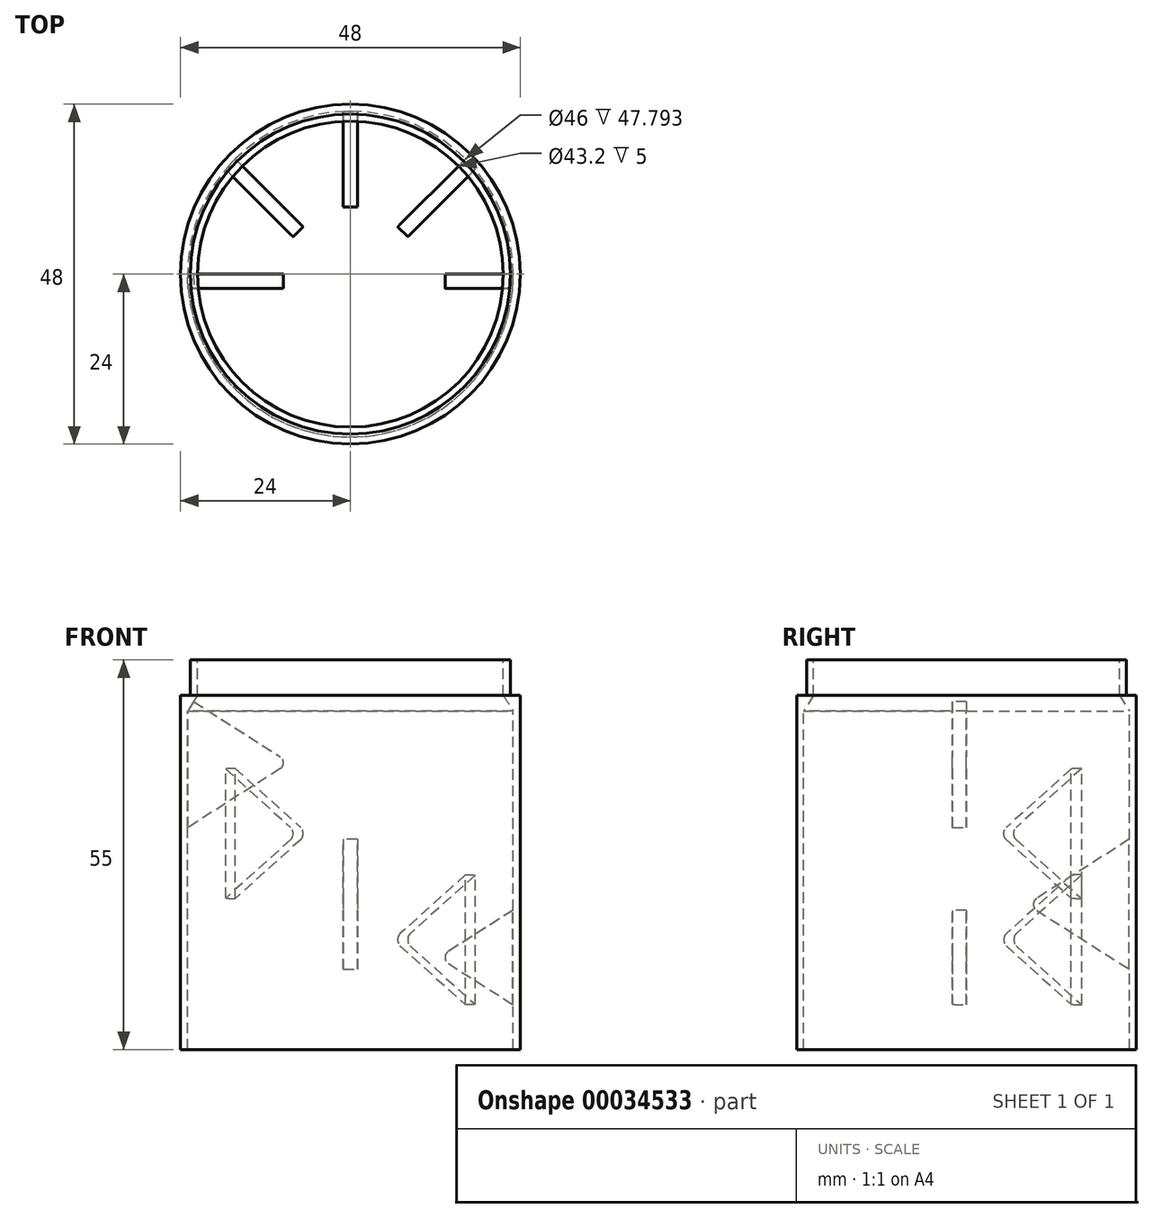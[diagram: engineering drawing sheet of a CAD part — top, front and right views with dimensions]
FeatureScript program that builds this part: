
annotation { "Feature Type Name" : "Feature", "Feature Type Description" : "" }
export const myFeature = defineFeature(function(context is Context, id is Id, definition is map)
    precondition{}
    {
        {
            var Q0;
            Q0=qCreatedBy(makeId("Top.planeOp"),FACE);
            var sketch = newSketch(context, id + "F0", { "sketchPlane" : qUnion([Q0])});
            skCircle(sketch, "E0", {"center": v(0, 0) * mm, "radius": 24 * mm});
            skSolve(sketch);
        }
        {
            var Q0;
            Q0=makeQuery(id+"F0.imprint","IMPRINT",FACE,{"disambiguationData":[TD([[makeQuery(id+"F0.imprint","IMPRINT",EDGE,{"derivedFrom":sQuery(id+"F0.wireOp",EDGE,"E0")}),1.0]])]});
            extrude(context, id + "F1", {"entities" : qUnion([Q0]), "depth" : 50 * mm});
        }
        {
            var Q0;
            Q0=makeQuery(id+"F1.opExtrude","CAP_FACE",FACE,{"disambiguationData":[OSD([sQuery(id+"F0.wireOp",EDGE,"E0")])],"isStart":false});
            var sketch = newSketch(context, id + "F2", { "sketchPlane" : qUnion([Q0])});
            skCircle(sketch, "E1", {"center": v(0, 0) * mm, "radius": 23 * mm});
            skSolve(sketch);
        }
        {
            var Q0;
            Q0=qSketchRegion(id+"F2",true);
            extrude(context, id + "F3", {"entities" : qUnion([Q0]), "operationType" : NewBodyOperationType.REMOVE, "endBound" : BoundingType.THROUGH_ALL, "oppositeDirection" : true, "depth" : 25 * mm});
        }
        {
            var Q0;
            Q0=qCreatedBy(makeId("Front.planeOp"),FACE);
            var sketch = newSketch(context, id + "F4", { "sketchPlane" : qUnion([Q0])});
            skLineSegment(sketch, "E2", {"start": v(0, 0) * mm, "end": v(0, 50) * mm});
            skLineSegment(sketch, "E3.0", {"start": v(-23.5, 50) * mm, "end": v(-23.5, 47) * mm});
            skLineSegment(sketch, "E4", {"start": v(-23.5, 50) * mm, "end": v(-22.6, 50) * mm});
            skLineSegment(sketch, "E5", {"start": v(-22.6, 50) * mm, "end": v(-22.6, 55) * mm});
            skLineSegment(sketch, "E6", {"start": v(-22.6, 55) * mm, "end": v(-21.6, 55) * mm});
            skLineSegment(sketch, "E7", {"start": v(-21.6, 55) * mm, "end": v(-21.6, 50) * mm});
            skLineSegment(sketch, "E8", {"start": v(-21.6, 50) * mm, "end": v(-23.5, 47) * mm});
            skLineSegment(sketch, "E9", {"start": v(-24, 50) * mm, "end": v(-23.5, 50) * mm});
            skSolve(sketch);
        }
        {
            var Q0;
            Q0=qSketchRegion(id+"F4",true);
            var Q1;
            Q1=makeQuery(id+"F3.boolean.opBoolean","COPY",FACE,{"derivedFrom":makeQuery(id+"F3.opExtrude","SWEPT_FACE",FACE,{"disambiguationData":[OSD([sQuery(id+"F2.wireOp",EDGE,"E1")])]})});
            revolve(context, id + "F5", {"operationType" : NewBodyOperationType.ADD, "entities" : qUnion([Q0]), "axis" : qUnion([Q1]), "revolveType" : RevolveType.FULL});
        }
        {
            var Q0;
            Q0=qCreatedBy(makeId("Right.planeOp"),FACE);
            var sketch = newSketch(context, id + "F6", { "sketchPlane" : qUnion([Q0])});
            skCircle(sketch, "E10", {"center": v(0, 27.55) * mm, "radius": 3 * mm});
            skLineSegment(sketch, "E11.rect.bottom", {"start": v(-3, 21.55) * mm, "end": v(3, 21.55) * mm});
            skLineSegment(sketch, "E11.rect.top", {"start": v(-3, 27.55) * mm, "end": v(3, 27.55) * mm});
            skLineSegment(sketch, "E11.rect.left", {"start": v(-3, 21.55) * mm, "end": v(-3, 27.55) * mm});
            skLineSegment(sketch, "E11.rect.right", {"start": v(3, 21.55) * mm, "end": v(3, 27.55) * mm});
            skPoint(sketch, "E11.rect.middle", {"position": v(0, 24.55) * mm});
            skSolve(sketch);
        }
        {
            var Q0;
            Q0=qCreatedBy(makeId("Front.planeOp"),FACE);
            var sketch = newSketch(context, id + "F7", { "sketchPlane" : qUnion([Q0])});
            skLineSegment(sketch, "E12", {"start": v(0, 0) * mm, "end": v(0, 55) * mm, "construction": true});
            skPoint(sketch, "E13", {"position": v(0, 55) * mm});
            skSolve(sketch);
        }
        {
            var Q0;
            Q0=qCreatedBy(makeId("Top.planeOp"),FACE);
            var sketch = newSketch(context, id + "F8", { "sketchPlane" : qUnion([Q0])});
            skLineSegment(sketch, "E14", {"start": v(0, 0) * mm, "end": v(-23.5, 0) * mm, "construction": true});
            skLineSegment(sketch, "E15", {"start": v(0, 0) * mm, "end": v(-16.62, 16.62) * mm, "construction": true});
            skLineSegment(sketch, "E16", {"start": v(0, 0) * mm, "end": v(0, 23.5) * mm, "construction": true});
            skLineSegment(sketch, "E17.MirrorCS", {"start": v(0, 0) * mm, "end": v(16.62, 16.62) * mm, "construction": true});
            skLineSegment(sketch, "E18.MirrorCS", {"start": v(0, 0) * mm, "end": v(23.5, 0) * mm, "construction": true});
            skSolve(sketch);
        }
        {
            var Q0;
            Q0=qCreatedBy(makeId("Front.planeOp"),FACE);
            var sketch = newSketch(context, id + "F9", { "sketchPlane" : qUnion([Q0])});
            skLineSegment(sketch, "E19", {"start": v(-23.5, 50) * mm, "end": v(-8.59, 40.5) * mm});
            skLineSegment(sketch, "E20", {"start": v(-8.59, 40.5) * mm, "end": v(-23.5, 31) * mm});
            skLineSegment(sketch, "E21", {"start": v(-23.5, 31) * mm, "end": v(-23.5, 50) * mm});
            skLineSegment(sketch, "E22", {"start": v(-8.59, 40.5) * mm, "end": v(-23.5, 40.5) * mm, "construction": true});
            skPoint(sketch, "E23.0", {"position": v(-23.5, 0) * mm});
            skLineSegment(sketch, "E24", {"start": v(-23.5, 0) * mm, "end": v(-23.5, 50) * mm, "construction": true});
            skPoint(sketch, "E25.0", {"position": v(23.5, 0) * mm});
            skLineSegment(sketch, "E26", {"start": v(23.5, 0) * mm, "end": v(23.5, 20) * mm, "construction": true});
            skLineSegment(sketch, "E27", {"start": v(23.5, 20) * mm, "end": v(23.5, 6) * mm});
            skLineSegment(sketch, "E28", {"start": v(23.5, 20) * mm, "end": v(12.51, 13) * mm});
            skLineSegment(sketch, "E29", {"start": v(12.51, 13) * mm, "end": v(23.5, 6) * mm});
            skLineSegment(sketch, "E30", {"start": v(23.5, 13) * mm, "end": v(12.51, 13) * mm, "construction": true});
            skSolve(sketch);
        }
        {
            var Q0;
            Q0=makeQuery(id+"F9.imprint","IMPRINT",FACE,{"disambiguationData":[TD([[makeQuery(id+"F9.imprint","IMPRINT",EDGE,{"derivedFrom":sQuery(id+"F9.wireOp",EDGE,"E19")}),-1.0]])]});
            var Q1;
            Q1=makeQuery(id+"F9.imprint","IMPRINT",FACE,{"disambiguationData":[TD([[makeQuery(id+"F9.imprint","IMPRINT",EDGE,{"derivedFrom":sQuery(id+"F9.wireOp",EDGE,"E27")}),-1.0]])]});
            extrude(context, id + "F10", {"entities" : qUnion([Q0, Q1]), "operationType" : NewBodyOperationType.ADD, "depth" : 2 * mm});
        }
        {
            var Q0;
            Q0=sQuery(id+"F8.wireOp",VERTEX,"E15.end");
            var Q1;
            Q1=sQuery(id+"F7.wireOp",VERTEX,"E13");
            var Q2;
            Q2=sQuery(id+"F7.wireOp",VERTEX,"E12.start");
            cPlane(context, id + "F11", {"entities" : qUnion([Q0, Q1, Q2]), "cplaneType" : CPlaneType.THREE_POINT, "offset" : 150 * mm, "width" : 150 * mm, "height" : 150 * mm});
        }
        {
            var Q0;
            Q0=qCreatedBy(id+"F11.planeOp",FACE);
            var sketch = newSketch(context, id + "F12", { "sketchPlane" : qUnion([Q0])});
            skLineSegment(sketch, "E31", {"start": v(-23.5, 40) * mm, "end": v(-23.5, 21) * mm});
            skLineSegment(sketch, "E32", {"start": v(-23.5, 40) * mm, "end": v(-8.59, 30.5) * mm});
            skLineSegment(sketch, "E33", {"start": v(-8.59, 30.5) * mm, "end": v(-23.5, 21) * mm});
            skLineSegment(sketch, "E34", {"start": v(-23.5, 30.5) * mm, "end": v(-8.59, 30.5) * mm, "construction": true});
            skLineSegment(sketch, "E35", {"start": v(-23.5, 0) * mm, "end": v(-23.5, 40) * mm, "construction": true});
            skSolve(sketch);
        }
        {
            var Q0;
            Q0 = qSketchRegion(id + "F12", true);
            extrude(context, id + "F13", {"entities" : qUnion([Q0]), "operationType" : NewBodyOperationType.ADD, "depth" : 2 * mm});
        }
        {
            var Q0;
            Q0=sQuery(id+"F7.wireOp",VERTEX,"E13");
            var Q1;
            Q1=sQuery(id+"F8.wireOp",VERTEX,"E16.end");
            var Q2;
            Q2=sQuery(id+"F7.wireOp",VERTEX,"E12.start");
            cPlane(context, id + "F14", {"entities" : qUnion([Q0, Q1, Q2]), "cplaneType" : CPlaneType.THREE_POINT, "offset" : 150 * mm, "width" : 150 * mm, "height" : 150 * mm});
        }
        {
            var Q0;
            Q0=qCreatedBy(id+"F14.planeOp",FACE);
            var sketch = newSketch(context, id + "F15", { "sketchPlane" : qUnion([Q0])});
            skLineSegment(sketch, "E36", {"start": v(23.5, 30) * mm, "end": v(23.5, 11) * mm});
            skLineSegment(sketch, "E37", {"start": v(23.5, 30) * mm, "end": v(8.59, 20.5) * mm});
            skLineSegment(sketch, "E38", {"start": v(8.59, 20.5) * mm, "end": v(23.5, 11) * mm});
            skLineSegment(sketch, "E39", {"start": v(23.5, 20.5) * mm, "end": v(8.59, 20.5) * mm, "construction": true});
            skLineSegment(sketch, "E40", {"start": v(23.5, 0) * mm, "end": v(23.5, 30) * mm, "construction": true});
            skSolve(sketch);
        }
        {
            var Q0;
            Q0 = qSketchRegion(id + "F15", true);
            extrude(context, id + "F16", {"entities" : qUnion([Q0]), "operationType" : NewBodyOperationType.ADD, "oppositeDirection" : true, "depth" : 1 * mm, "hasSecondDirection" : true, "secondDirectionOppositeDirection" : false, "secondDirectionDepth" : 1 * mm});
        }
        {
            var Q0;
            Q0=sQuery(id+"F7.wireOp",VERTEX,"E12.start");
            var Q1;
            Q1=sQuery(id+"F7.wireOp",VERTEX,"E13");
            var Q2;
            Q2=sQuery(id+"F8.wireOp",VERTEX,"E17.MirrorCS.end");
            cPlane(context, id + "F17", {"entities" : qUnion([Q0, Q1, Q2]), "cplaneType" : CPlaneType.THREE_POINT, "offset" : 150 * mm, "width" : 150 * mm, "height" : 150 * mm});
        }
        {
            var Q0;
            Q0=qCreatedBy(id+"F17.planeOp",FACE);
            var sketch = newSketch(context, id + "F18", { "sketchPlane" : qUnion([Q0])});
            skLineSegment(sketch, "E41", {"start": v(24, 50) * mm, "end": v(24, 0) * mm, "construction": true});
            skPoint(sketch, "E42", {"position": v(24, 12.5) * mm});
            skLineSegment(sketch, "E43", {"start": v(24, 12.5) * mm, "end": v(23.5, 12.5) * mm, "construction": true});
            skLineSegment(sketch, "E44", {"start": v(23.5, 25) * mm, "end": v(23.5, 6) * mm});
            skLineSegment(sketch, "E45", {"start": v(0, 0) * mm, "end": v(23.5, 0) * mm, "construction": true});
            skLineSegment(sketch, "E46", {"start": v(23.5, 0) * mm, "end": v(23.5, 6) * mm, "construction": true});
            skLineSegment(sketch, "E47", {"start": v(23.5, 25) * mm, "end": v(8.59, 15.5) * mm});
            skLineSegment(sketch, "E48", {"start": v(23.5, 15.5) * mm, "end": v(8.59, 15.5) * mm, "construction": true});
            skLineSegment(sketch, "E49", {"start": v(8.59, 15.5) * mm, "end": v(23.5, 6) * mm});
            skSolve(sketch);
        }
        {
            var Q0;
            Q0 = qSketchRegion(id + "F18", true);
            extrude(context, id + "F19", {"entities" : qUnion([Q0]), "operationType" : NewBodyOperationType.ADD, "depth" : 2 * mm});
        }
        {
            var Q0;
            Q0=makeQuery(id+"F10.opExtrude","SWEPT_EDGE",EDGE,{"disambiguationData":[OSD([sQuery(id+"F9.wireOp",EDGE,"E19"),sQuery(id+"F9.wireOp",EDGE,"E20")])]});
            var Q1;
            Q1=makeQuery(id+"F13.opExtrude","SWEPT_EDGE",EDGE,{"disambiguationData":[OSD([sQuery(id+"F12.wireOp",EDGE,"E32"),sQuery(id+"F12.wireOp",EDGE,"E33")])]});
            var Q2;
            Q2=makeQuery(id+"F16.opExtrude","SWEPT_EDGE",EDGE,{"disambiguationData":[OSD([sQuery(id+"F15.wireOp",EDGE,"E37"),sQuery(id+"F15.wireOp",EDGE,"E38")])]});
            var Q3;
            Q3=makeQuery(id+"F19.opExtrude","SWEPT_EDGE",EDGE,{"disambiguationData":[OSD([sQuery(id+"F18.wireOp",EDGE,"E47"),sQuery(id+"F18.wireOp",EDGE,"E49")])]});
            var Q4;
            Q4=makeQuery(id+"F10.opExtrude","SWEPT_EDGE",EDGE,{"disambiguationData":[OSD([sQuery(id+"F9.wireOp",EDGE,"E28"),sQuery(id+"F9.wireOp",EDGE,"E29")])]});
            fillet(context, id + "F20", {"entities" : qUnion([Q0, Q1, Q2, Q3, Q4]), "radius" : 1 * mm, "tangentPropagation" : true, "allowEdgeOverflow" : false});
        }
    });
